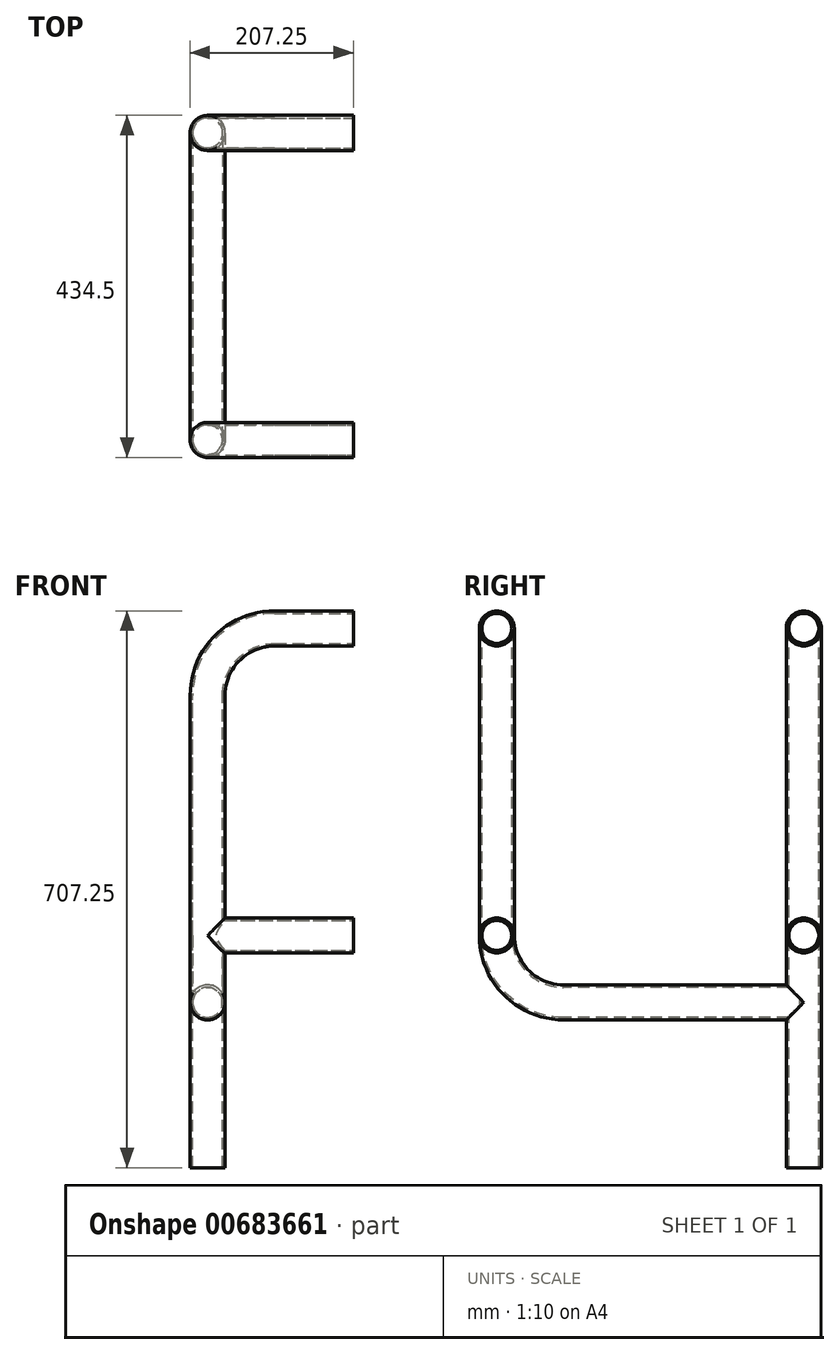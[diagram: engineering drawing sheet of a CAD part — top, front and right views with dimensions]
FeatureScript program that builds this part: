
annotation { "Feature Type Name" : "Feature", "Feature Type Description" : "" }
export const myFeature = defineFeature(function(context is Context, id is Id, definition is map)
    precondition{}
    {
        {
            var Q0;
            Q0=qCreatedBy(makeId("Front.planeOp"),FACE);
            var sketch = newSketch(context, id + "F0", { "sketchPlane" : qUnion([Q0])});
            skLineSegment(sketch, "E0", {"start": v(0, 0) * mm, "end": v(0, 600) * mm});
            skLineSegment(sketch, "E1", {"start": v(0, 600) * mm, "end": v(0, 600) * mm});
            skLineSegment(sketch, "E2", {"start": v(85, 685) * mm, "end": v(185, 685) * mm});
            skPoint(sketch, "E3.visualSharp", {"position": v(0, 685) * mm});
            skArc(sketch, "E3.filletArc", {"start": v(85, 685) * mm, "mid": v(24.9, 660.1) * mm, "end": v(0, 600) * mm});
            skSolve(sketch);
        }
        {
            var Q0;
            Q0=qCreatedBy(makeId("Top.planeOp"),FACE);
            var sketch = newSketch(context, id + "F1", { "sketchPlane" : qUnion([Q0])});
            skCircle(sketch, "E4", {"center": v(0, 0) * mm, "radius": 22.25 * mm});
            skCircle(sketch, "E5.0", {"center": v(0, 0) * mm, "radius": 19.05 * mm});
            skSolve(sketch);
        }
        {
            var Q0;
            Q0=makeQuery(id+"F1.imprint","IMPRINT",FACE,{"disambiguationData":[TD([[makeQuery(id+"F1.imprint","IMPRINT",EDGE,{"derivedFrom":sQuery(id+"F1.wireOp",EDGE,"E4")}),1.0]])]});
            var Q1;
            Q1=sQuery(id+"F0.wireOp",EDGE,"E0");
            var Q2;
            Q2=sQuery(id+"F0.wireOp",EDGE,"E3.filletArc");
            var Q3;
            Q3=sQuery(id+"F0.wireOp",EDGE,"E2");
            sweep(context, id + "F2", {"profiles" : qUnion([Q0]), "path" : qUnion([Q1, Q2, Q3])});
        }
        {
            var Q0;
            Q0=qCreatedBy(makeId("Right.planeOp"),FACE);
            cPlane(context, id + "F3", {"entities" : qUnion([Q0]), "cplaneType" : CPlaneType.OFFSET, "offset" : 185 * mm, "width" : 150 * mm, "height" : 150 * mm});
        }
        {
            var Q0;
            Q0=qCreatedBy(id+"F3.planeOp",FACE);
            var sketch = newSketch(context, id + "F4", { "sketchPlane" : qUnion([Q0])});
            skCircle(sketch, "E6", {"center": v(0, 295) * mm, "radius": 22.25 * mm});
            skCircle(sketch, "E7.0", {"center": v(0, 295) * mm, "radius": 19.05 * mm});
            skSolve(sketch);
        }
        {
            var Q0;
            Q0=makeQuery(id+"F4.imprint","IMPRINT",FACE,{"disambiguationData":[TD([[makeQuery(id+"F4.imprint","IMPRINT",EDGE,{"derivedFrom":sQuery(id+"F4.wireOp",EDGE,"E6")}),1.0]])]});
            var Q1;
            Q1=makeQuery(id+"F2.opSweep","SWEPT_BODY",BODY,{"disambiguationData":[OSD([sQuery(id+"F0.wireOp",EDGE,"E2"),sQuery(id+"F1.wireOp",EDGE,"E4"),sQuery(id+"F1.wireOp",EDGE,"E5.0")])]});
            extrude(context, id + "F5", {"entities" : qUnion([Q0]), "endBound" : BoundingType.UP_TO_BODY, "oppositeDirection" : true, "depth" : 185 * mm, "endBoundEntityBody" : qUnion([Q1]), "offsetDistance" : 25 * mm});
        }
        {
            var Q0;
            Q0=makeQuery(id+"F5.opExtrude","CAP_FACE",FACE,{"disambiguationData":[OSD([sQuery(id+"F4.wireOp",EDGE,"E6"),sQuery(id+"F4.wireOp",EDGE,"E7.0")])],"isStart":true});
            var sketch = newSketch(context, id + "F6", { "sketchPlane" : qUnion([Q0])});
            skCircle(sketch, "E8.0", {"center": v(0, 295) * mm, "radius": 19.05 * mm});
            skSolve(sketch);
        }
        {
            var Q0;
            Q0=makeQuery(id+"F6.imprint","IMPRINT",FACE,{"disambiguationData":[TD([[makeQuery(id+"F6.imprint","IMPRINT",EDGE,{"derivedFrom":sQuery(id+"F6.wireOp",EDGE,"E8.0")}),1.0]])]});
            var Q1;
            Q1=makeQuery(id+"F2.opSweep","SWEPT_BODY",BODY,{"disambiguationData":[OSD([sQuery(id+"F0.wireOp",EDGE,"E2"),sQuery(id+"F1.wireOp",EDGE,"E4"),sQuery(id+"F1.wireOp",EDGE,"E5.0")])]});
            extrude(context, id + "F7", {"entities" : qUnion([Q0]), "operationType" : NewBodyOperationType.REMOVE, "oppositeDirection" : true, "depth" : 185 * mm, "endBoundEntityBody" : qUnion([Q1]), "offsetDistance" : 25 * mm});
        }
        {
            var Q0;
            Q0=qCreatedBy(makeId("Front.planeOp"),FACE);
            cPlane(context, id + "F8", {"entities" : qUnion([Q0]), "cplaneType" : CPlaneType.OFFSET, "offset" : 305 * mm, "width" : 150 * mm, "height" : 150 * mm});
        }
        {
            var Q0;
            Q0=qCreatedBy(id+"F8.planeOp",FACE);
            var sketch = newSketch(context, id + "F9", { "sketchPlane" : qUnion([Q0])});
            skCircle(sketch, "E9", {"center": v(0, 210) * mm, "radius": 22.25 * mm});
            skCircle(sketch, "E10.0", {"center": v(0, 210) * mm, "radius": 19.05 * mm});
            skSolve(sketch);
        }
        {
            var Q0;
            Q0=makeQuery(id+"F9.imprint","IMPRINT",FACE,{"disambiguationData":[TD([[makeQuery(id+"F9.imprint","IMPRINT",EDGE,{"derivedFrom":sQuery(id+"F9.wireOp",EDGE,"E9")}),1.0]])]});
            var Q1;
            Q1=makeQuery(id+"F2.opSweep","SWEPT_BODY",BODY,{"disambiguationData":[OSD([sQuery(id+"F0.wireOp",EDGE,"E2"),sQuery(id+"F1.wireOp",EDGE,"E4"),sQuery(id+"F1.wireOp",EDGE,"E5.0")])]});
            extrude(context, id + "F10", {"entities" : qUnion([Q0]), "operationType" : NewBodyOperationType.ADD, "endBound" : BoundingType.UP_TO_BODY, "oppositeDirection" : true, "depth" : 25 * mm, "endBoundEntityBody" : qUnion([Q1]), "offsetDistance" : 25 * mm});
        }
        {
            var Q0;
            Q0=makeQuery(id+"F10.opExtrude","CAP_FACE",FACE,{"disambiguationData":[OSD([sQuery(id+"F9.wireOp",EDGE,"E9"),sQuery(id+"F9.wireOp",EDGE,"E10.0")])],"isStart":true});
            var sketch = newSketch(context, id + "F11", { "sketchPlane" : qUnion([Q0])});
            skCircle(sketch, "E11.0", {"center": v(0, 210) * mm, "radius": 19.05 * mm});
            skSolve(sketch);
        }
        {
            var Q0;
            Q0 = qSketchRegion(id + "F11", true);
            var Q1;
            Q1=makeQuery(id+"F2.opSweep","SWEPT_BODY",BODY,{"disambiguationData":[OSD([sQuery(id+"F0.wireOp",EDGE,"E2"),sQuery(id+"F1.wireOp",EDGE,"E4"),sQuery(id+"F1.wireOp",EDGE,"E5.0")])]});
            extrude(context, id + "F12", {"entities" : qUnion([Q0]), "operationType" : NewBodyOperationType.REMOVE, "oppositeDirection" : true, "depth" : 300 * mm, "endBoundEntityBody" : qUnion([Q1]), "offsetDistance" : 25 * mm});
        }
        {
            var Q0;
            Q0=qCreatedBy(makeId("Right.planeOp"),FACE);
            var sketch = newSketch(context, id + "F13", { "sketchPlane" : qUnion([Q0])});
            skLineSegment(sketch, "E12.0", {"start": v(-305, 187.75) * mm, "end": v(-305, 232.25) * mm});
            skLineSegment(sketch, "E13", {"start": v(-305, 210) * mm, "end": v(-305, 210) * mm});
            skLineSegment(sketch, "E14", {"start": v(-390, 295) * mm, "end": v(-390, 600) * mm});
            skPoint(sketch, "E15.visualSharp", {"position": v(-390, 210) * mm});
            skArc(sketch, "E15.filletArc", {"start": v(-390, 295) * mm, "mid": v(-365.1, 234.9) * mm, "end": v(-305, 210) * mm});
            skSolve(sketch);
        }
        {
            var Q0;
            Q0=makeQuery(id+"F10.opExtrude","CAP_FACE",FACE,{"disambiguationData":[OSD([sQuery(id+"F9.wireOp",EDGE,"E9"),sQuery(id+"F9.wireOp",EDGE,"E10.0")])],"isStart":true});
            var Q1;
            Q1=sQuery(id+"F13.wireOp",EDGE,"E15.filletArc");
            var Q2;
            Q2=sQuery(id+"F13.wireOp",EDGE,"E14");
            sweep(context, id + "F14", {"operationType" : NewBodyOperationType.ADD, "profiles" : qUnion([Q0]), "path" : qUnion([Q1, Q2])});
        }
        {
            var Q0;
            Q0=qCreatedBy(makeId("Front.planeOp"),FACE);
            cPlane(context, id + "F15", {"entities" : qUnion([Q0]), "cplaneType" : CPlaneType.OFFSET, "offset" : 390 * mm, "width" : 150 * mm, "height" : 150 * mm});
        }
        {
            var Q0;
            Q0=qCreatedBy(id+"F15.planeOp",FACE);
            var sketch = newSketch(context, id + "F16", { "sketchPlane" : qUnion([Q0])});
            skLineSegment(sketch, "E16.0", {"start": v(-22.25, 600) * mm, "end": v(22.25, 600) * mm});
            skLineSegment(sketch, "E17.0", {"start": v(85, 707.25) * mm, "end": v(85, 662.75) * mm});
            skArc(sketch, "E18", {"start": v(85, 685) * mm, "mid": v(24.9, 660.1) * mm, "end": v(0, 600) * mm});
            skLineSegment(sketch, "E19", {"start": v(85, 685) * mm, "end": v(185, 685) * mm});
            skSolve(sketch);
        }
        {
            var Q0;
            Q0=makeQuery(id+"F14.opSweep","CAP_FACE",FACE,{"disambiguationData":[OSD([sQuery(id+"F9.wireOp",EDGE,"E9"),sQuery(id+"F9.wireOp",EDGE,"E10.0"),sQuery(id+"F13.wireOp",VERTEX,"E14.end")])],"isStart":false});
            var Q1;
            Q1=sQuery(id+"F16.wireOp",EDGE,"E18");
            var Q2;
            Q2=sQuery(id+"F16.wireOp",EDGE,"E19");
            sweep(context, id + "F17", {"operationType" : NewBodyOperationType.ADD, "profiles" : qUnion([Q0]), "path" : qUnion([Q1, Q2])});
        }
        {
            var Q0;
            Q0=qCreatedBy(id+"F3.planeOp",FACE);
            var sketch = newSketch(context, id + "F18", { "sketchPlane" : qUnion([Q0])});
            skCircle(sketch, "E20.0", {"center": v(0, 295) * mm, "radius": 19.05 * mm});
            skCircle(sketch, "E21", {"center": v(-390, 295) * mm, "radius": 22.25 * mm});
            skCircle(sketch, "E22.0", {"center": v(-390, 295) * mm, "radius": 19.05 * mm});
            skSolve(sketch);
        }
        {
            var Q0;
            Q0=makeQuery(id+"F18.imprint","IMPRINT",FACE,{"disambiguationData":[TD([[makeQuery(id+"F18.imprint","IMPRINT",EDGE,{"derivedFrom":sQuery(id+"F18.wireOp",EDGE,"E21")}),1.0]])]});
            var Q1;
            Q1=makeQuery(id+"F2.opSweep","SWEPT_BODY",BODY,{"disambiguationData":[OSD([sQuery(id+"F0.wireOp",EDGE,"E2"),sQuery(id+"F1.wireOp",EDGE,"E4"),sQuery(id+"F1.wireOp",EDGE,"E5.0")])]});
            extrude(context, id + "F19", {"entities" : qUnion([Q0]), "operationType" : NewBodyOperationType.ADD, "endBound" : BoundingType.UP_TO_BODY, "oppositeDirection" : true, "depth" : 25 * mm, "endBoundEntityBody" : qUnion([Q1]), "offsetDistance" : 25 * mm});
        }
        {
            var Q0;
            Q0=makeQuery(id+"F19.opExtrude","CAP_FACE",FACE,{"disambiguationData":[OSD([sQuery(id+"F18.wireOp",EDGE,"E21"),sQuery(id+"F18.wireOp",EDGE,"E22.0")])],"isStart":true});
            var sketch = newSketch(context, id + "F20", { "sketchPlane" : qUnion([Q0])});
            skCircle(sketch, "E23.0", {"center": v(-390, 295) * mm, "radius": 19.05 * mm});
            skSolve(sketch);
        }
        {
            var Q0;
            Q0=makeQuery(id+"F20.imprint","IMPRINT",FACE,{"disambiguationData":[TD([[makeQuery(id+"F20.imprint","IMPRINT",EDGE,{"derivedFrom":sQuery(id+"F20.wireOp",EDGE,"E23.0")}),1.0]])]});
            var Q1;
            Q1=makeQuery(id+"F19.boolean.opBoolean","SPLIT",FACE,{"disambiguationData":[TD([makeQuery(id+"F19.opExtrude","SWEPT_FACE",FACE,{"disambiguationData":[OSD([sQuery(id+"F18.wireOp",EDGE,"E22.0")])]})])],"derivedFrom":makeQuery(id+"F14.opSweep","SWEPT_FACE",FACE,{"disambiguationData":[OSD([sQuery(id+"F9.wireOp",EDGE,"E9"),sQuery(id+"F13.wireOp",EDGE,"E14")])]})});
            var Q2;
            Q2=makeQuery(id+"F2.opSweep","SWEPT_BODY",BODY,{"disambiguationData":[OSD([sQuery(id+"F0.wireOp",EDGE,"E2"),sQuery(id+"F1.wireOp",EDGE,"E4"),sQuery(id+"F1.wireOp",EDGE,"E5.0")])]});
            extrude(context, id + "F21", {"entities" : qUnion([Q0]), "operationType" : NewBodyOperationType.REMOVE, "oppositeDirection" : true, "depth" : 185 * mm, "endBoundEntityFace" : qUnion([Q1]), "endBoundEntityBody" : qUnion([Q2]), "offsetDistance" : 25 * mm});
        }
    });
